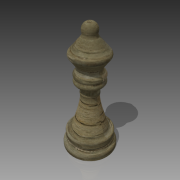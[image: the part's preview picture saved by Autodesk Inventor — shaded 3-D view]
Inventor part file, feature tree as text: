
AUTODESK INVENTOR PART (.ipt)
format: ipt  version: 2015 SP1 (Build 190203100, 203)  size: 347,136 bytes
history: native  units: mm
features: fillet x3, revolve x1, sketch x1
ambient origin geometry x8: Origin, YZ Plane, XZ Plane, XY Plane, X Axis, Y Axis, Z Axis, Center Point
bodies: Solid1 (feature_tree)
feature tree (5):
  revolve  "Revolution1"  [1 undecoded]
  fillet  "Fillet3"  Radius=1.0mm
  fillet  "Fillet4"  Radius=2.0mm
  fillet  "Fillet5"  Radius=70.0mm
  sketch  "Sketch1"  dims[d10=90.0deg d11=2.0mm d13=1.0mm d24=2.0mm d34=70.0mm d35=2.0mm d36=2.0mm d37=2.0mm d38=2.0mm]
note: 1 required parameter value undecoded (feature->parameter linkage not recoverable at this tier; creation-order binding heuristic only, values carry confidence <= 0.55)
